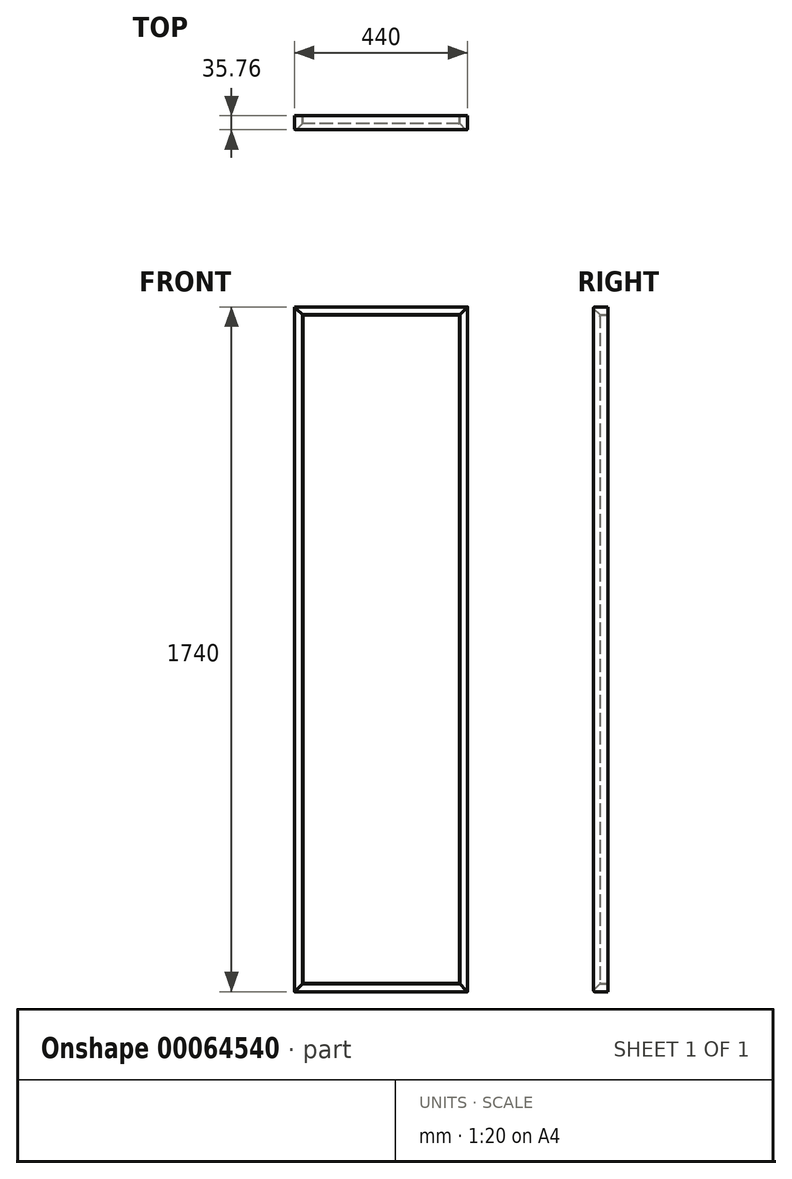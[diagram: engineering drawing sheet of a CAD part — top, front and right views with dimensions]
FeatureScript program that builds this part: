
annotation { "Feature Type Name" : "Feature", "Feature Type Description" : "" }
export const myFeature = defineFeature(function(context is Context, id is Id, definition is map)
    precondition{}
    {
        {
            var Q0;
            Q0=qCreatedBy(makeId("Front.planeOp"),FACE);
            var sketch = newSketch(context, id + "F0", { "sketchPlane" : qUnion([Q0])});
            skLineSegment(sketch, "E0.bottom", {"start": v(-62.83, 1643.37) * mm, "end": v(377.17, 1643.37) * mm});
            skLineSegment(sketch, "E0.top", {"start": v(-62.83, -96.63) * mm, "end": v(377.17, -96.63) * mm});
            skLineSegment(sketch, "E0.left", {"start": v(-62.83, 1643.37) * mm, "end": v(-62.83, -96.63) * mm});
            skLineSegment(sketch, "E0.right", {"start": v(377.17, 1643.37) * mm, "end": v(377.17, -96.63) * mm});
            skLineSegment(sketch, "E1.bottom", {"start": v(-42.83, 1623.37) * mm, "end": v(357.17, 1623.37) * mm});
            skLineSegment(sketch, "E1.top", {"start": v(-42.83, -76.63) * mm, "end": v(357.17, -76.63) * mm});
            skLineSegment(sketch, "E1.left", {"start": v(-42.83, 1623.37) * mm, "end": v(-42.83, -76.63) * mm});
            skLineSegment(sketch, "E1.right", {"start": v(357.17, 1623.37) * mm, "end": v(357.17, -76.63) * mm});
            skSolve(sketch);
        }
        {
            var Q0;
            Q0=makeQuery(id+"F0.imprint","IMPRINT",FACE,{"disambiguationData":[TD([[makeQuery(id+"F0.imprint","IMPRINT",EDGE,{"derivedFrom":sQuery(id+"F0.wireOp",EDGE,"E0.bottom")}),-1.0]])]});
            extrude(context, id + "F1", {"entities" : qUnion([Q0]), "depth" : 40 * mm});
        }
        {
            var Q0;
            Q0=makeQuery(id+"F1.opExtrude","CAP_EDGE",EDGE,{"disambiguationData":[OSD([sQuery(id+"F0.wireOp",EDGE,"E1.right")])],"isStart":false});
            var Q1;
            Q1=makeQuery(id+"F1.opExtrude","CAP_EDGE",EDGE,{"disambiguationData":[OSD([sQuery(id+"F0.wireOp",EDGE,"E1.bottom")])],"isStart":false});
            var Q2;
            Q2=makeQuery(id+"F1.opExtrude","CAP_EDGE",EDGE,{"disambiguationData":[OSD([sQuery(id+"F0.wireOp",EDGE,"E1.left")])],"isStart":false});
            var Q3;
            Q3=makeQuery(id+"F1.opExtrude","CAP_EDGE",EDGE,{"disambiguationData":[OSD([sQuery(id+"F0.wireOp",EDGE,"E1.top")])],"isStart":false});
            chamfer(context, id + "F2", {"entities" : qUnion([Q0, Q1, Q2, Q3]), "width" : 20 * mm, "tangentPropagation" : true});
        }
        {
            var Q0;
            Q0=makeQuery(id+"F2.opChamfer","BLEND_EDGE",EDGE,{"blendedFrom":[makeQuery(id+"F1.opExtrude","CAP_EDGE",EDGE,{"disambiguationData":[OSD([sQuery(id+"F0.wireOp",EDGE,"E1.left")])],"isStart":false}),makeQuery(id+"F1.opExtrude","SWEPT_FACE",FACE,{"disambiguationData":[OSD([sQuery(id+"F0.wireOp",EDGE,"E0.left")])]})],"blendedInto":[makeQuery(id+"F1.opExtrude","SWEPT_FACE",FACE,{"disambiguationData":[OSD([sQuery(id+"F0.wireOp",EDGE,"E0.left")])]})]});
            var Q1;
            Q1=makeQuery(id+"F2.opChamfer","BLEND_EDGE",EDGE,{"blendedFrom":[makeQuery(id+"F1.opExtrude","CAP_EDGE",EDGE,{"disambiguationData":[OSD([sQuery(id+"F0.wireOp",EDGE,"E1.right")])],"isStart":false}),makeQuery(id+"F1.opExtrude","SWEPT_FACE",FACE,{"disambiguationData":[OSD([sQuery(id+"F0.wireOp",EDGE,"E0.right")])]})],"blendedInto":[makeQuery(id+"F1.opExtrude","SWEPT_FACE",FACE,{"disambiguationData":[OSD([sQuery(id+"F0.wireOp",EDGE,"E0.right")])]})]});
            var Q2;
            Q2=makeQuery(id+"F2.opChamfer","BLEND_EDGE",EDGE,{"blendedFrom":[makeQuery(id+"F1.opExtrude","CAP_EDGE",EDGE,{"disambiguationData":[OSD([sQuery(id+"F0.wireOp",EDGE,"E1.bottom")])],"isStart":false}),makeQuery(id+"F1.opExtrude","SWEPT_FACE",FACE,{"disambiguationData":[OSD([sQuery(id+"F0.wireOp",EDGE,"E0.bottom")])]})],"blendedInto":[makeQuery(id+"F1.opExtrude","SWEPT_FACE",FACE,{"disambiguationData":[OSD([sQuery(id+"F0.wireOp",EDGE,"E0.bottom")])]})]});
            var Q3;
            Q3=makeQuery(id+"F2.opChamfer","BLEND_EDGE",EDGE,{"blendedFrom":[makeQuery(id+"F1.opExtrude","CAP_EDGE",EDGE,{"disambiguationData":[OSD([sQuery(id+"F0.wireOp",EDGE,"E1.top")])],"isStart":false}),makeQuery(id+"F1.opExtrude","SWEPT_FACE",FACE,{"disambiguationData":[OSD([sQuery(id+"F0.wireOp",EDGE,"E0.top")])]})],"blendedInto":[makeQuery(id+"F1.opExtrude","SWEPT_FACE",FACE,{"disambiguationData":[OSD([sQuery(id+"F0.wireOp",EDGE,"E0.top")])]})]});
            fillet(context, id + "F3", {"entities" : qUnion([Q0, Q1, Q2, Q3]), "radius" : 3 * mm, "tangentPropagation" : true, "allowEdgeOverflow" : false});
        }
        {
            var Q0;
            Q0=makeQuery(id+"F1.opExtrude","CAP_FACE",FACE,{"disambiguationData":[OSD([sQuery(id+"F0.wireOp",EDGE,"E0.bottom"),sQuery(id+"F0.wireOp",EDGE,"E0.top"),sQuery(id+"F0.wireOp",EDGE,"E0.left"),sQuery(id+"F0.wireOp",EDGE,"E0.right"),sQuery(id+"F0.wireOp",EDGE,"E1.bottom"),sQuery(id+"F0.wireOp",EDGE,"E1.top"),sQuery(id+"F0.wireOp",EDGE,"E1.left"),sQuery(id+"F0.wireOp",EDGE,"E1.right")])],"isStart":true});
            var sketch = newSketch(context, id + "F4", { "sketchPlane" : qUnion([Q0])});
            skLineSegment(sketch, "E2.bottom", {"start": v(-356.17, 1622.37) * mm, "end": v(41.83, 1622.37) * mm});
            skLineSegment(sketch, "E2.top", {"start": v(-356.17, -75.63) * mm, "end": v(41.83, -75.63) * mm});
            skLineSegment(sketch, "E2.left", {"start": v(-356.17, 1622.37) * mm, "end": v(-356.17, -75.63) * mm});
            skLineSegment(sketch, "E2.right", {"start": v(41.83, 1622.37) * mm, "end": v(41.83, -75.63) * mm});
            skSolve(sketch);
        }
        {
            var Q0;
            Q0=makeQuery(id+"F4.imprint","IMPRINT",FACE,{"disambiguationData":[TD([[makeQuery(id+"F4.imprint","IMPRINT",EDGE,{"derivedFrom":sQuery(id+"F4.wireOp",EDGE,"E2.bottom")}),-1.0]])]});
            extrude(context, id + "F5", {"entities" : qUnion([Q0]), "oppositeDirection" : true, "depth" : 20 * mm});
        }
        {
            var Q0;
            Q0=makeQuery(id+"F5.opExtrude","CAP_EDGE",EDGE,{"disambiguationData":[OSD([sQuery(id+"F4.wireOp",EDGE,"E2.right")])],"isStart":false});
            var Q1;
            Q1=makeQuery(id+"F5.opExtrude","CAP_EDGE",EDGE,{"disambiguationData":[OSD([sQuery(id+"F4.wireOp",EDGE,"E2.left")])],"isStart":false});
            var Q2;
            Q2=makeQuery(id+"F5.opExtrude","CAP_EDGE",EDGE,{"disambiguationData":[OSD([sQuery(id+"F4.wireOp",EDGE,"E2.bottom")])],"isStart":false});
            var Q3;
            Q3=makeQuery(id+"F5.opExtrude","CAP_EDGE",EDGE,{"disambiguationData":[OSD([sQuery(id+"F4.wireOp",EDGE,"E2.top")])],"isStart":false});
            fillet(context, id + "F6", {"entities" : qUnion([Q0, Q1, Q2, Q3]), "radius" : 3 * mm, "tangentPropagation" : true, "allowEdgeOverflow" : false});
        }
    });
